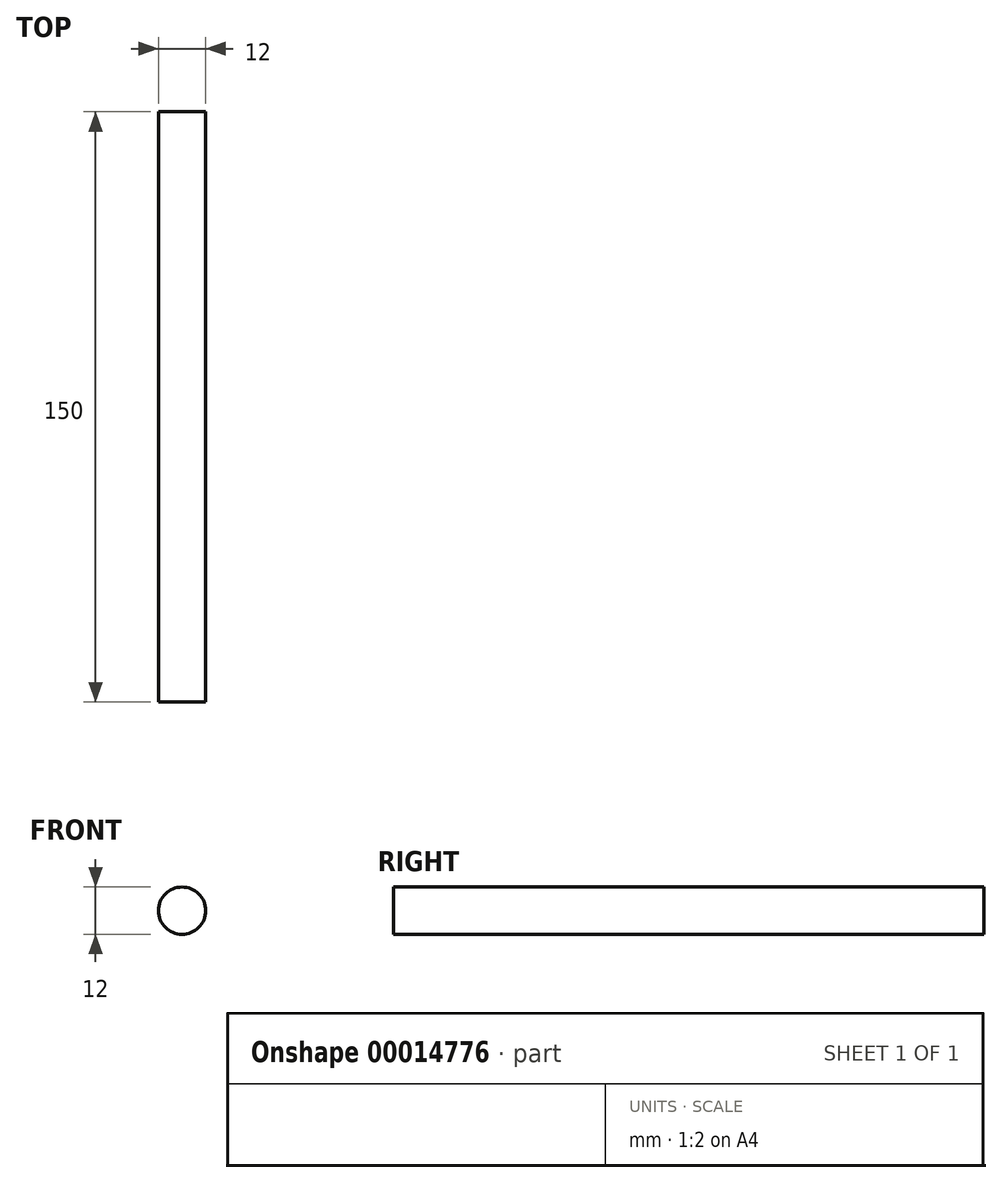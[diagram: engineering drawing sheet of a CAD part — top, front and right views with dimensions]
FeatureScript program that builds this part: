
annotation { "Feature Type Name" : "Feature", "Feature Type Description" : "" }
export const myFeature = defineFeature(function(context is Context, id is Id, definition is map)
    precondition{}
    {
        {
            var Q0;
            Q0=qCreatedBy(makeId("Front.planeOp"),FACE);
            var sketch = newSketch(context, id + "F0", { "sketchPlane" : qUnion([Q0])});
            skCircle(sketch, "E0", {"center": v(0, 0) * mm, "radius": 6 * mm});
            skSolve(sketch);
        }
        {
            var Q0;
            Q0=makeQuery(id+"F0.imprint","IMPRINT",FACE,{"disambiguationData":[TD([[makeQuery(id+"F0.imprint","IMPRINT",EDGE,{"derivedFrom":sQuery(id+"F0.wireOp",EDGE,"E0")}),1.0]])]});
            var Q1;
            Q1=sQuery(id+"F0.wireOp",EDGE,"E0");
            extrude(context, id + "F1", {"entities" : qUnion([Q0]), "surfaceEntities" : qUnion([Q1]), "endBound" : BoundingType.SYMMETRIC, "depth" : 150 * mm});
        }
    });
